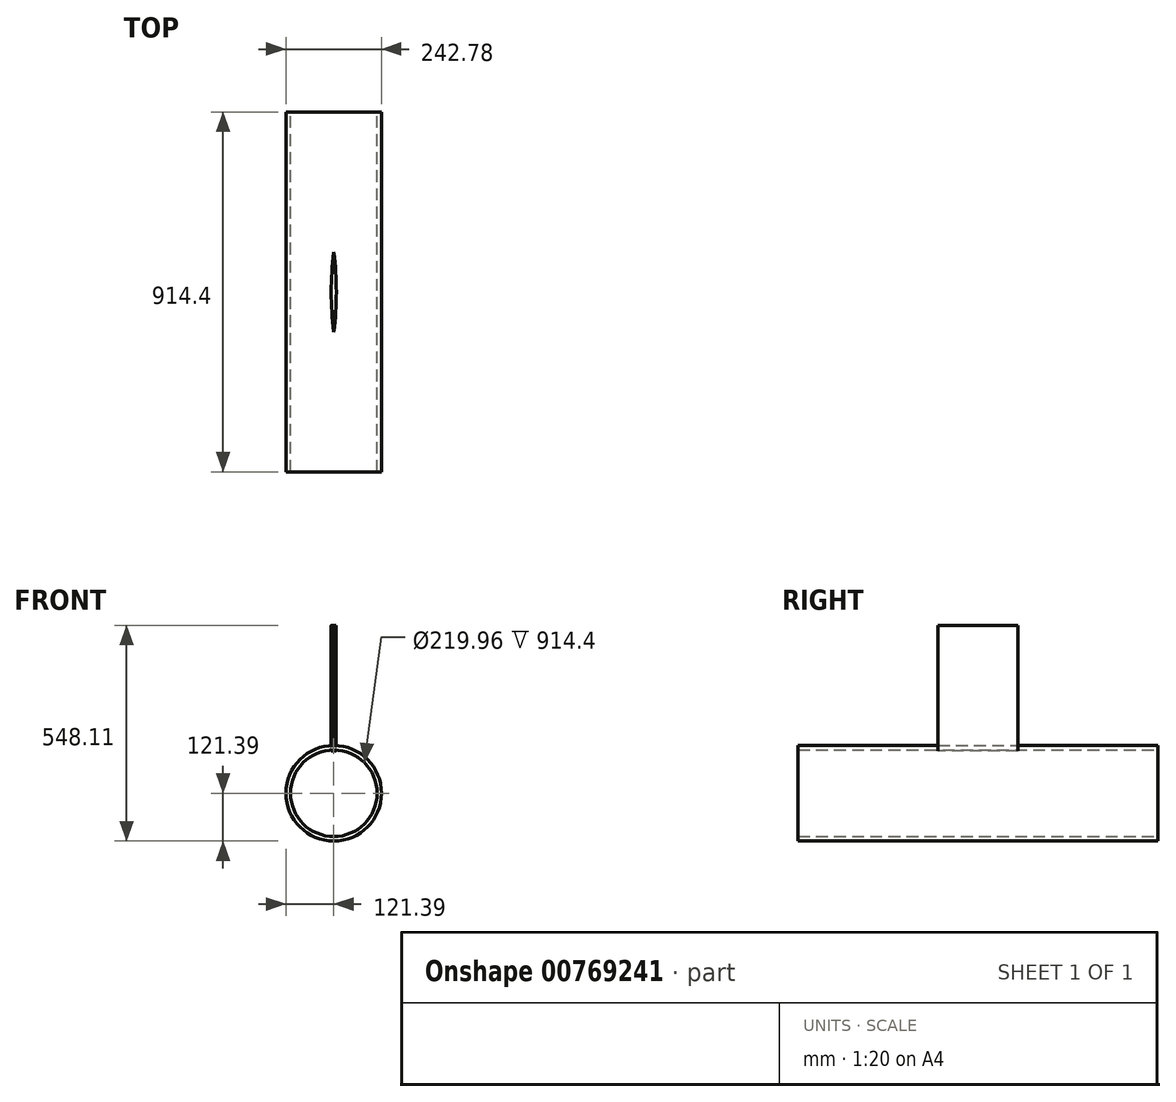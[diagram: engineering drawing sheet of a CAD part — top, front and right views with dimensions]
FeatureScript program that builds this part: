
annotation { "Feature Type Name" : "Feature", "Feature Type Description" : "" }
export const myFeature = defineFeature(function(context is Context, id is Id, definition is map)
    precondition{}
    {
        {
            var Q0;
            Q0=qCreatedBy(makeId("Front.planeOp"),FACE);
            var sketch = newSketch(context, id + "F0", { "sketchPlane" : qUnion([Q0])});
            skCircle(sketch, "E0", {"center": v(0, 0) * mm, "radius": 121.39 * mm});
            skCircle(sketch, "E1", {"center": v(0, 0) * mm, "radius": 109.98 * mm});
            skSolve(sketch);
        }
        {
            var Q0;
            Q0=makeQuery(id+"F0.imprint","IMPRINT",FACE,{"disambiguationData":[TD([[makeQuery(id+"F0.imprint","IMPRINT",EDGE,{"derivedFrom":sQuery(id+"F0.wireOp",EDGE,"E0")}),1.0]])]});
            extrude(context, id + "F1", {"entities" : qUnion([Q0]), "flatOperationType" : FlatOperationType.REMOVE, "depth" : 914.4 * mm, "offsetDistance" : 25.4 * mm, "domain" : OperationDomain.MODEL, "symmetric" : true});
        }
        {
            var Q0;
            Q0=qCreatedBy(makeId("Top.planeOp"),FACE);
            cPlane(context, id + "F2", {"entities" : qUnion([Q0]), "cplaneType" : CPlaneType.OFFSET, "offset" : 426.72 * mm, "width" : 152.4 * mm, "height" : 152.4 * mm});
        }
        {
            var Q0;
            Q0=qCreatedBy(id+"F2.planeOp",FACE);
            var sketch = newSketch(context, id + "F3", { "sketchPlane" : qUnion([Q0])});
            skLineSegment(sketch, "E2", {"start": v(0, 101.6) * mm, "end": v(0, -101.6) * mm});
            skArc(sketch, "E3", {"start": v(0, -101.6) * mm, "mid": v(6.5, 0) * mm, "end": v(0, 101.6) * mm});
            skArc(sketch, "E4.MirrorCS", {"start": v(0, -101.6) * mm, "mid": v(-6.5, 0) * mm, "end": v(0, 101.6) * mm});
            skSolve(sketch);
        }
        {
            var Q0;
            Q0=makeQuery(id+"F3.imprint","IMPRINT",FACE,{"disambiguationData":[TD([[makeQuery(id+"F3.imprint","IMPRINT",EDGE,{"derivedFrom":sQuery(id+"F3.wireOp",EDGE,"E2")}),-1.0]])]});
            var Q1;
            Q1=makeQuery(id+"F3.imprint","IMPRINT",FACE,{"disambiguationData":[TD([[makeQuery(id+"F3.imprint","IMPRINT",EDGE,{"derivedFrom":sQuery(id+"F3.wireOp",EDGE,"E2")}),1.0]])]});
            extrude(context, id + "F4", {"entities" : qUnion([Q0, Q1]), "flatOperationType" : FlatOperationType.REMOVE, "oppositeDirection" : true, "depth" : 318.52 * mm, "offsetDistance" : 25.4 * mm, "domain" : OperationDomain.MODEL});
        }
    });
